# Revit family: RN 85179 Optiflex-Profix-Wanddurchführungswinkel
name_source: partatom
category: Rohrformteile
units: mm (PartAtom-declared; Revit-internal decimal feet)

## family parameters
Arbeitsebenenbasiert = Nein
Beim Laden mit Abzugskörper schneiden = Nein
Bemaßung runder Anschluss = Durchmesser verwenden
Gemeinsam genutzt = Nein
Immer vertikal = Ja
Teiletyp = Bogen

## types (3) — shared parameters
1.010.00.2 Blattnummer der Richtlinie = 29
1.010.00.3 Ausgabedatum (Monat) der Richtlinie = 201308
1.010.00.4 Herstellername = R. Nussbaum AG
1.010.00.5 Revisionsdatum der Datei = 20190521
1.010.00.6 Webadresse des Herstellers = http://www.nussbaum.ch
1.100.00.4 Produktbezeichnung = Versorgung
1.110.00.2 Index = 5
1.110.00.4 Produktbezeichnung = Optiflex
1.960/3L.00.8 Link (URL) = https://www.nussbaum.ch
29.700.00.4 Produktname = Optiflex-Profix-Wanddurchführungswinkel
29.700.00.5 Produktkennung = 2
29.700.00.6 Querschnittsform = 1
29.700.00.7 Nennweitensystem = DN
29.700.00.8 Nenndrucksystem = PN
29.710.02.4 Nenndruck = 10
29.710.02.5 max. zul. Überdruck [hPa] = 1000
29.710.02.7 max. zul. Dauer-Betriebsdruck [hPa] = 1000
29.710.02.9 max. zul. Dauer-Betriebstemperatur [°C] = 70
CONNECTOR0_dZ_01 = 34 mm  [stored 0.111549 ft]
CONNECTOR0_ref_dZ = 34 mm  [stored 0.111549 ft]
CONNECTOR1_DIAMETER_dX_0r = 15 mm
CONNECTOR1_ref_dZ = 63 mm  [stored 0.206693 ft]
Connector Visibility = Nein
EnclosingSpace Visibility = Nein
Hersteller = R. Nussbaum AG
R. Nussbaum AG 85179.22 de Visibility = Nein
URL = https://www.nussbaum.ch

## per-type parameters (varying)
| type | 1.800.00.3 TGA-Nummer | 1.800.00.4 Kommentarfeld | 1.810.00.3 Hersteller-Bestellnummer | 1.810.00.4 DATANORM-Nummer | 1.810.00.6 GTIN-Nummer | 29.710.02.10 Formstück-Gewicht [kg] | 29.710.02.3 Benennung | CONNECTOR0_DIAMETER_dZ_0r | CONNECTOR1_dX_00 | CONNECTOR1_dX_01 | CONNECTOR1_ref_dX | Modell | R. Nussbaum AG 85179.21 de Visibility | R. Nussbaum AG 85179.23 de Visibility | Typenkommentare |
| DN=15 | 01900500000000000000000000000000000000000000000095000000000000000003 | 85179.23, Optiflex-Profix-Wanddurchführungswinkel, DN=15, L=63, Rp=½ | 85179.23 | 85179.23 | 7612945818447 | 0.299 | Optiflex-Profix-Wanddurchführungswinkel, DN=15, L=63, Rp=½ | 15 mm | 68 mm | 81 mm | 68 mm | 85179.23 | Nein | Ja | Optiflex-Profix-Wanddurchführungswinkel  DN=15 |
| DN=12x15 | 01900500000000000000000000000000000000000000000095000000000000000001 | 85179.21, Optiflex-Profix-Wanddurchführungswinkel, DN=12x15, L=63, Rp=½ | 85179.21 | 85179.21 | 7612945818423 | 0.258 | Optiflex-Profix-Wanddurchführungswinkel, DN=12x15, L=63, Rp=½ | 12 mm  [stored 0.0393701 ft] | 48 mm | 61 mm | 48 mm | 85179.21 | Ja | Nein | Optiflex-Profix-Wanddurchführungswinkel  DN=12x15 |
| DN=12x1 | 01900500000000000000000000000000000000000000000095000000000000000001 | 85179.21, Optiflex-Profix-Wanddurchführungswinkel, DN=12x15, L=63, Rp=½ | 85179.21 | 85179.21 | 7612945818423 | 0.258 | Optiflex-Profix-Wanddurchführungswinkel, DN=12x15, L=63, Rp=½ | 12 mm  [stored 0.0393701 ft] | 48 mm | 61 mm | 48 mm | 85179.21 | Ja | Nein | Optiflex-Profix-Wanddurchführungswinkel  DN=12x15 |

note: [stored X ft] marks values corroborated as IEEE doubles in the binary element streams (Revit-internal decimal feet)

## geometry (parser evidence)
native form markers: Sweep x3
no freeform markers — native parametric forms only
